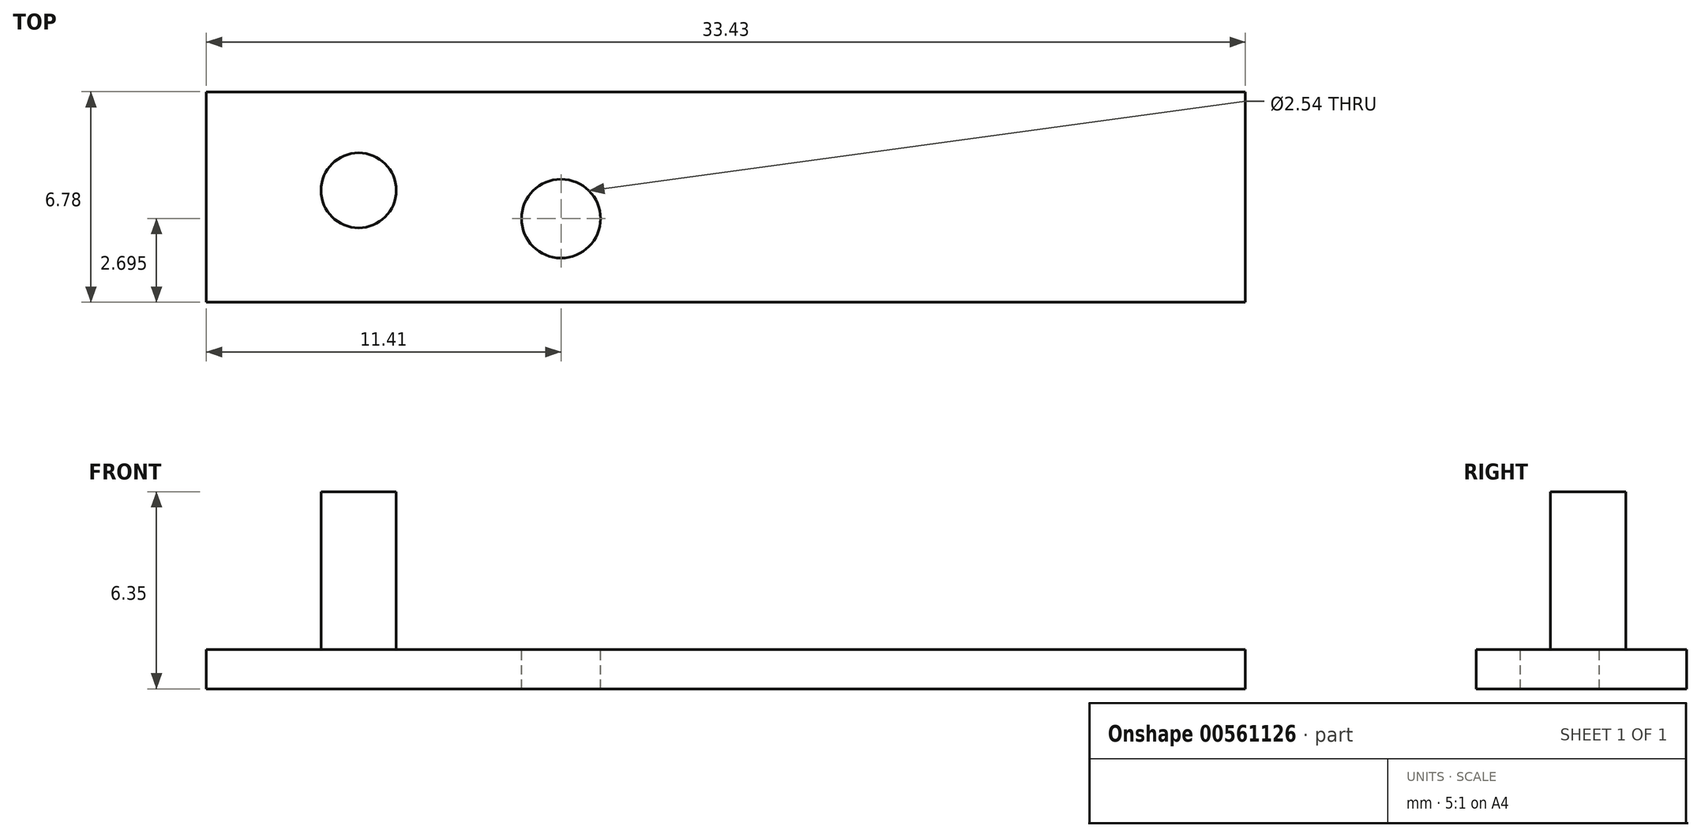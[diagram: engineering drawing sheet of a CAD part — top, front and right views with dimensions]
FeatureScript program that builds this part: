
annotation { "Feature Type Name" : "Feature", "Feature Type Description" : "" }
export const myFeature = defineFeature(function(context is Context, id is Id, definition is map)
    precondition{}
    {
        {
            var Q0;
            Q0=qCreatedBy(makeId("Top.planeOp"),FACE);
            var sketch = newSketch(context, id + "F0", { "sketchPlane" : qUnion([Q0])});
            skLineSegment(sketch, "E0.bottom", {"start": v(-48.82, -58.24) * mm, "end": v(-15.4, -58.24) * mm});
            skLineSegment(sketch, "E0.top", {"start": v(-48.82, -51.46) * mm, "end": v(-15.4, -51.46) * mm});
            skLineSegment(sketch, "E0.left", {"start": v(-48.82, -58.24) * mm, "end": v(-48.82, -51.46) * mm});
            skLineSegment(sketch, "E0.right", {"start": v(-15.4, -58.24) * mm, "end": v(-15.4, -51.46) * mm});
            skSolve(sketch);
        }
        {
            var Q0;
            Q0=makeQuery(id+"F0.imprint","IMPRINT",FACE,{"disambiguationData":[TD([[makeQuery(id+"F0.imprint","IMPRINT",EDGE,{"derivedFrom":sQuery(id+"F0.wireOp",EDGE,"E0.bottom")}),1.0]])]});
            extrude(context, id + "F1", {"entities" : qUnion([Q0]), "depth" : 1.27 * mm, "offsetDistance" : 25.4 * mm});
        }
        {
            var Q0;
            Q0=makeQuery(id+"F1.opExtrude","CAP_FACE",FACE,{"disambiguationData":[OSD([sQuery(id+"F0.wireOp",EDGE,"E0.bottom"),sQuery(id+"F0.wireOp",EDGE,"E0.top"),sQuery(id+"F0.wireOp",EDGE,"E0.left"),sQuery(id+"F0.wireOp",EDGE,"E0.right")])],"isStart":false});
            var sketch = newSketch(context, id + "F2", { "sketchPlane" : qUnion([Q0])});
            skCircle(sketch, "E1", {"center": v(-37.41, -55.55) * mm, "radius": 1.91 * mm});
            skSolve(sketch);
        }
        {
            var Q0;
            Q0=sQuery(id+"F2.wireOp",VERTEX,"E1.center");
            var Q1;
            Q1=makeQuery(id+"F1.opExtrude","SWEPT_BODY",BODY,{"disambiguationData":[OSD([sQuery(id+"F0.wireOp",EDGE,"E0.bottom"),sQuery(id+"F0.wireOp",EDGE,"E0.top"),sQuery(id+"F0.wireOp",EDGE,"E0.left"),sQuery(id+"F0.wireOp",EDGE,"E0.right")])]});
            hole(context, id + "F3", {"style" : HoleStyle.SIMPLE, "endStyle" : HoleEndStyle.THROUGH, "holeDiameter" : 2.54 * mm, "isTappedThrough" : true, "tappedDepth" : 12.7 * mm, "tapClearance" : 3, "locations" : qUnion([Q0]), "scope" : qUnion([Q1])});
        }
        {
            var Q0;
            Q0=makeQuery(id+"F1.opExtrude","CAP_FACE",FACE,{"disambiguationData":[OSD([sQuery(id+"F0.wireOp",EDGE,"E0.bottom"),sQuery(id+"F0.wireOp",EDGE,"E0.top"),sQuery(id+"F0.wireOp",EDGE,"E0.left"),sQuery(id+"F0.wireOp",EDGE,"E0.right")])],"isStart":false});
            var sketch = newSketch(context, id + "F4", { "sketchPlane" : qUnion([Q0])});
            skCircle(sketch, "E2", {"center": v(-37.41, -55.55) * mm, "radius": 1.12 * mm});
            skSolve(sketch);
        }
        {
            var Q0;
            Q0=makeQuery(id+"F4.imprint","IMPRINT",FACE,{"disambiguationData":[TD([[makeQuery(id+"F4.imprint","IMPRINT",EDGE,{"derivedFrom":sQuery(id+"F4.wireOp",EDGE,"E2")}),1.0]])]});
            extrude(context, id + "F5", {"entities" : qUnion([Q0]), "depth" : 5.77 * mm, "offsetDistance" : 25.4 * mm});
        }
        {
            var Q0;
            Q0=makeQuery(id+"F5.opExtrude","SWEPT_BODY",BODY,{"disambiguationData":[OSD([sQuery(id+"F4.wireOp",EDGE,"E2")])]});
            deleteBodies(context, id + "F6", {"entities" : qUnion([Q0])});
        }
        {
            var Q0;
            Q0=makeQuery(id+"F1.opExtrude","CAP_FACE",FACE,{"disambiguationData":[OSD([sQuery(id+"F0.wireOp",EDGE,"E0.bottom"),sQuery(id+"F0.wireOp",EDGE,"E0.top"),sQuery(id+"F0.wireOp",EDGE,"E0.left"),sQuery(id+"F0.wireOp",EDGE,"E0.right")])],"isStart":false});
            var sketch = newSketch(context, id + "F7", { "sketchPlane" : qUnion([Q0])});
            skCircle(sketch, "E3", {"center": v(-43.92, -54.64) * mm, "radius": 1.2 * mm});
            skSolve(sketch);
        }
        {
            var Q0;
            Q0=makeQuery(id+"F7.imprint","IMPRINT",FACE,{"disambiguationData":[TD([[makeQuery(id+"F7.imprint","IMPRINT",EDGE,{"derivedFrom":sQuery(id+"F7.wireOp",EDGE,"E3")}),1.0]])]});
            extrude(context, id + "F8", {"entities" : qUnion([Q0]), "operationType" : NewBodyOperationType.ADD, "depth" : 5.08 * mm, "offsetDistance" : 25.4 * mm});
        }
    });
